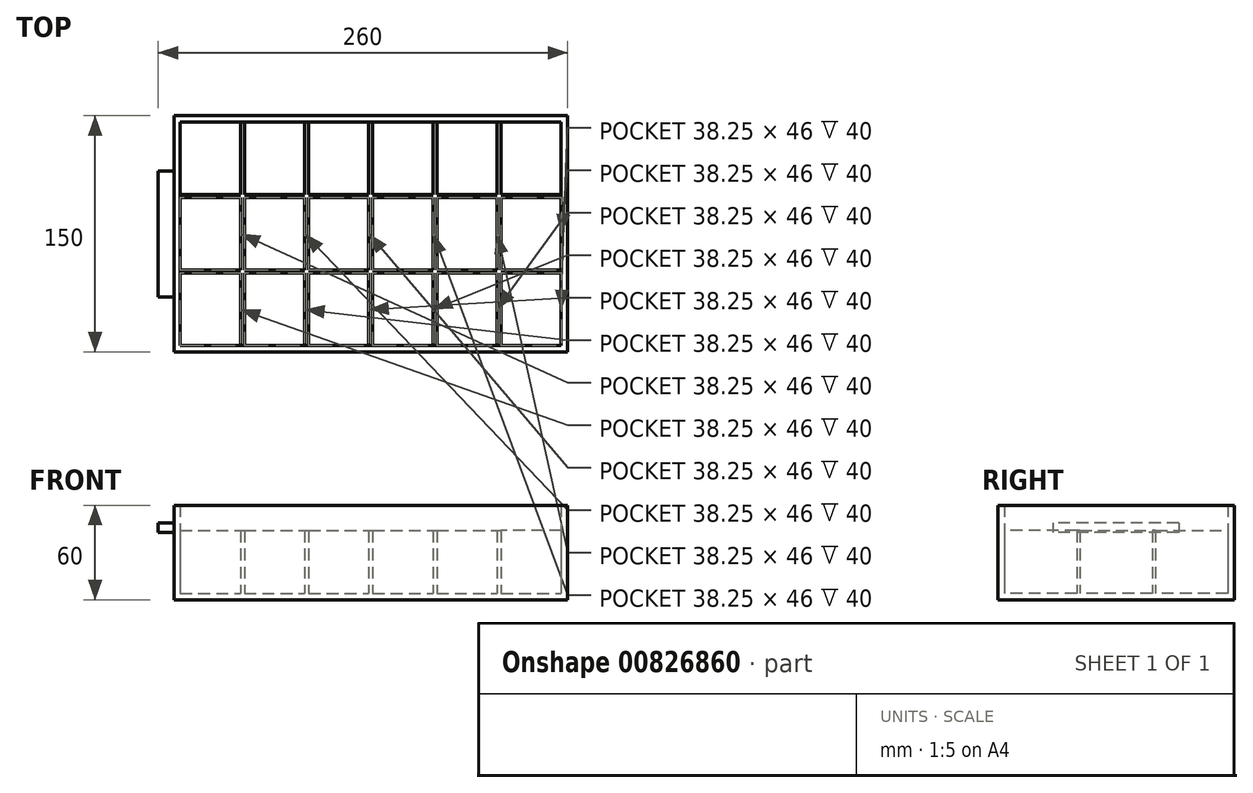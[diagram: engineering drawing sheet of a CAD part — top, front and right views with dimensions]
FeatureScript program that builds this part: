
annotation { "Feature Type Name" : "Feature", "Feature Type Description" : "" }
export const myFeature = defineFeature(function(context is Context, id is Id, definition is map)
    precondition{}
    {
        {
            var Q0;
            Q0=qCreatedBy(makeId("Top.planeOp"),FACE);
            var sketch = newSketch(context, id + "F0", { "sketchPlane" : qUnion([Q0])});
            skLineSegment(sketch, "E0.bottom", {"start": v(-124.11, 65.2) * mm, "end": v(125.89, 65.2) * mm});
            skLineSegment(sketch, "E0.top", {"start": v(-124.11, -84.8) * mm, "end": v(125.89, -84.8) * mm});
            skLineSegment(sketch, "E0.left", {"start": v(-124.11, 65.2) * mm, "end": v(-124.11, -84.8) * mm});
            skLineSegment(sketch, "E0.right", {"start": v(125.89, 65.2) * mm, "end": v(125.89, -84.8) * mm});
            skSolve(sketch);
        }
        {
            var Q0;
            Q0=makeQuery(id+"F0.imprint","IMPRINT",FACE,{"disambiguationData":[TD([[makeQuery(id+"F0.imprint","IMPRINT",EDGE,{"derivedFrom":sQuery(id+"F0.wireOp",EDGE,"E0.bottom")}),-1.0]])]});
            extrude(context, id + "F1", {"entities" : qUnion([Q0]), "depth" : 60 * mm, "offsetDistance" : 25 * mm});
        }
        {
            var Q0;
            Q0=makeQuery(id+"F1.opExtrude","CAP_FACE",FACE,{"disambiguationData":[OSD([sQuery(id+"F0.wireOp",EDGE,"E0.bottom"),sQuery(id+"F0.wireOp",EDGE,"E0.top"),sQuery(id+"F0.wireOp",EDGE,"E0.left"),sQuery(id+"F0.wireOp",EDGE,"E0.right")])],"isStart":false});
            shell(context, id + "F2", {"entities" : qUnion([Q0]), "thickness" : 4 * mm});
        }
        {
            var Q0;
            Q0=makeQuery(id+"F2.opShell","OFFSET_FACE",FACE,{"disambiguationData":[OSD([sQuery(id+"F0.wireOp",EDGE,"E0.bottom"),sQuery(id+"F0.wireOp",EDGE,"E0.top"),sQuery(id+"F0.wireOp",EDGE,"E0.left"),sQuery(id+"F0.wireOp",EDGE,"E0.right")])]});
            var sketch = newSketch(context, id + "F3", { "sketchPlane" : qUnion([Q0])});
            skLineSegment(sketch, "E1", {"start": v(-120.11, 15.2) * mm, "end": v(-81.86, 15.2) * mm});
            skLineSegment(sketch, "E2", {"start": v(-120.11, 13.2) * mm, "end": v(-81.86, 13.2) * mm});
            skLineSegment(sketch, "E3", {"start": v(-120.11, -32.8) * mm, "end": v(-81.86, -32.8) * mm});
            skLineSegment(sketch, "E4", {"start": v(121.89, -32.8) * mm, "end": v(121.89, -34.8) * mm});
            skLineSegment(sketch, "E5", {"start": v(121.89, -34.8) * mm, "end": v(83.64, -34.8) * mm});
            skLineSegment(sketch, "E6", {"start": v(-120.11, -34.8) * mm, "end": v(-120.11, -32.8) * mm});
            skLineSegment(sketch, "E7", {"start": v(-120.11, 15.2) * mm, "end": v(-120.11, 13.2) * mm});
            skLineSegment(sketch, "E8", {"start": v(121.89, 15.2) * mm, "end": v(121.89, 13.2) * mm});
            skLineSegment(sketch, "E9", {"start": v(-81.86, 61.2) * mm, "end": v(-81.86, 15.2) * mm});
            skLineSegment(sketch, "E10", {"start": v(-81.86, -80.8) * mm, "end": v(-79.36, -80.8) * mm});
            skLineSegment(sketch, "E11", {"start": v(-79.36, -80.8) * mm, "end": v(-79.36, -34.8) * mm});
            skLineSegment(sketch, "E12", {"start": v(-79.36, 61.2) * mm, "end": v(-81.86, 61.2) * mm});
            skLineSegment(sketch, "E13", {"start": v(-41.11, 61.2) * mm, "end": v(-41.11, 15.2) * mm});
            skLineSegment(sketch, "E14", {"start": v(-41.11, -80.8) * mm, "end": v(-38.61, -80.8) * mm});
            skLineSegment(sketch, "E15", {"start": v(-38.61, -80.8) * mm, "end": v(-38.61, -34.8) * mm});
            skLineSegment(sketch, "E16", {"start": v(-38.61, 61.2) * mm, "end": v(-41.11, 61.2) * mm});
            skLineSegment(sketch, "E17", {"start": v(-0.36, 61.2) * mm, "end": v(-0.36, 15.2) * mm});
            skLineSegment(sketch, "E18", {"start": v(-0.36, -80.8) * mm, "end": v(2.14, -80.8) * mm});
            skLineSegment(sketch, "E19", {"start": v(2.14, -80.8) * mm, "end": v(2.14, -34.8) * mm});
            skLineSegment(sketch, "E20", {"start": v(2.14, 61.2) * mm, "end": v(-0.36, 61.2) * mm});
            skLineSegment(sketch, "E21", {"start": v(40.39, 61.2) * mm, "end": v(40.39, 15.2) * mm});
            skLineSegment(sketch, "E22", {"start": v(40.39, -80.8) * mm, "end": v(42.89, -80.8) * mm});
            skLineSegment(sketch, "E23", {"start": v(42.89, -80.8) * mm, "end": v(42.89, -34.8) * mm});
            skLineSegment(sketch, "E24", {"start": v(42.89, 61.2) * mm, "end": v(40.39, 61.2) * mm});
            skLineSegment(sketch, "E25", {"start": v(81.14, 61.2) * mm, "end": v(81.14, 15.2) * mm});
            skLineSegment(sketch, "E26", {"start": v(81.14, -80.8) * mm, "end": v(83.64, -80.8) * mm});
            skLineSegment(sketch, "E27", {"start": v(83.64, -80.8) * mm, "end": v(83.64, -34.8) * mm});
            skLineSegment(sketch, "E28", {"start": v(83.64, 61.2) * mm, "end": v(81.14, 61.2) * mm});
            skLineSegment(sketch, "E29", {"start": v(-81.86, 13.2) * mm, "end": v(-81.86, -32.8) * mm});
            skLineSegment(sketch, "E30", {"start": v(-79.36, 15.2) * mm, "end": v(-41.11, 15.2) * mm});
            skLineSegment(sketch, "E31", {"start": v(-79.36, 13.2) * mm, "end": v(-41.11, 13.2) * mm});
            skLineSegment(sketch, "E32.trimOffspring", {"start": v(-79.36, 15.2) * mm, "end": v(-79.36, 61.2) * mm});
            skLineSegment(sketch, "E33", {"start": v(-38.61, 15.2) * mm, "end": v(-0.36, 15.2) * mm});
            skLineSegment(sketch, "E34", {"start": v(-38.61, 13.2) * mm, "end": v(-0.36, 13.2) * mm});
            skLineSegment(sketch, "E35", {"start": v(2.14, 15.2) * mm, "end": v(2.15, 15.2) * mm});
            skLineSegment(sketch, "E36", {"start": v(2.15, 15.2) * mm, "end": v(40.39, 15.2) * mm});
            skLineSegment(sketch, "E37", {"start": v(-0.36, 13.2) * mm, "end": v(-0.36, -32.8) * mm});
            skLineSegment(sketch, "E38", {"start": v(2.14, 13.2) * mm, "end": v(40.39, 13.2) * mm});
            skLineSegment(sketch, "E39", {"start": v(40.39, 13.2) * mm, "end": v(40.39, -32.8) * mm});
            skLineSegment(sketch, "E40", {"start": v(42.89, 15.2) * mm, "end": v(81.14, 15.2) * mm});
            skLineSegment(sketch, "E41", {"start": v(42.89, 13.2) * mm, "end": v(81.14, 13.2) * mm});
            skLineSegment(sketch, "E42", {"start": v(83.64, 15.2) * mm, "end": v(121.89, 15.2) * mm});
            skLineSegment(sketch, "E43", {"start": v(83.64, 15.2) * mm, "end": v(83.64, 61.2) * mm});
            skLineSegment(sketch, "E44", {"start": v(83.64, 13.2) * mm, "end": v(121.89, 13.2) * mm});
            skLineSegment(sketch, "E45", {"start": v(83.64, -32.8) * mm, "end": v(121.89, -32.8) * mm});
            skLineSegment(sketch, "E46", {"start": v(81.14, -34.8) * mm, "end": v(81.14, -80.8) * mm});
            skLineSegment(sketch, "E47", {"start": v(81.14, -34.8) * mm, "end": v(42.89, -34.8) * mm});
            skLineSegment(sketch, "E48", {"start": v(42.89, -32.8) * mm, "end": v(81.14, -32.8) * mm});
            skLineSegment(sketch, "E49", {"start": v(42.89, -32.8) * mm, "end": v(42.89, 13.2) * mm});
            skLineSegment(sketch, "E50", {"start": v(40.39, -34.8) * mm, "end": v(40.39, -80.8) * mm});
            skLineSegment(sketch, "E51", {"start": v(2.14, -32.8) * mm, "end": v(40.39, -32.8) * mm});
            skLineSegment(sketch, "E52", {"start": v(-0.36, -34.8) * mm, "end": v(-38.61, -34.8) * mm});
            skLineSegment(sketch, "E53", {"start": v(-0.36, -34.8) * mm, "end": v(-0.36, -80.8) * mm});
            skLineSegment(sketch, "E54", {"start": v(-38.61, -32.8) * mm, "end": v(-0.36, -32.8) * mm});
            skLineSegment(sketch, "E55", {"start": v(-41.11, -34.8) * mm, "end": v(-79.36, -34.8) * mm});
            skLineSegment(sketch, "E56", {"start": v(-41.11, -34.8) * mm, "end": v(-41.11, -80.8) * mm});
            skLineSegment(sketch, "E57", {"start": v(-79.36, -32.8) * mm, "end": v(-41.11, -32.8) * mm});
            skLineSegment(sketch, "E58", {"start": v(-79.36, -32.8) * mm, "end": v(-79.36, 13.2) * mm});
            skLineSegment(sketch, "E59", {"start": v(-81.86, -34.8) * mm, "end": v(-120.11, -34.8) * mm});
            skLineSegment(sketch, "E60.trimOffspring", {"start": v(-81.86, -34.8) * mm, "end": v(-81.86, -80.8) * mm});
            skLineSegment(sketch, "E61.trimOffspring", {"start": v(-38.61, -32.8) * mm, "end": v(-38.61, 13.2) * mm});
            skLineSegment(sketch, "E62.trimOffspring", {"start": v(2.14, -32.8) * mm, "end": v(2.14, 13.2) * mm});
            skLineSegment(sketch, "E63.trimOffspring", {"start": v(40.39, -34.8) * mm, "end": v(2.14, -34.8) * mm});
            skLineSegment(sketch, "E64.trimOffspring", {"start": v(83.64, -32.8) * mm, "end": v(83.64, 13.2) * mm});
            skLineSegment(sketch, "E65.trimOffspring", {"start": v(81.14, 13.2) * mm, "end": v(81.14, -32.8) * mm});
            skLineSegment(sketch, "E66.trimOffspring", {"start": v(42.89, 15.2) * mm, "end": v(42.89, 61.2) * mm});
            skLineSegment(sketch, "E67.trimOffspring", {"start": v(2.14, 15.2) * mm, "end": v(2.14, 61.2) * mm});
            skLineSegment(sketch, "E68.trimOffspring", {"start": v(-41.11, 13.2) * mm, "end": v(-41.11, -32.8) * mm});
            skLineSegment(sketch, "E69.trimOffspring", {"start": v(-38.61, 15.2) * mm, "end": v(-38.61, 61.2) * mm});
            skSolve(sketch);
        }
        {
            var Q0;
            Q0=makeQuery(id+"F3.imprint","IMPRINT",FACE,{"disambiguationData":[TD([[makeQuery(id+"F3.imprint","IMPRINT",EDGE,{"derivedFrom":sQuery(id+"F3.wireOp",EDGE,"E1")}),-1.0]])]});
            extrude(context, id + "F4", {"entities" : qUnion([Q0]), "operationType" : NewBodyOperationType.ADD, "depth" : 40 * mm, "offsetDistance" : 25 * mm});
        }
        {
            var Q0;
            Q0=makeQuery(id+"F1.opExtrude","SWEPT_FACE",FACE,{"disambiguationData":[OSD([sQuery(id+"F0.wireOp",EDGE,"E0.left")])]});
            var sketch = newSketch(context, id + "F5", { "sketchPlane" : qUnion([Q0])});
            skLineSegment(sketch, "E70.bottom", {"start": v(-30, 48.68) * mm, "end": v(50, 48.68) * mm});
            skLineSegment(sketch, "E70.top", {"start": v(-30, 42.68) * mm, "end": v(50, 42.68) * mm});
            skLineSegment(sketch, "E70.left", {"start": v(-30, 48.68) * mm, "end": v(-30, 42.68) * mm});
            skLineSegment(sketch, "E70.right", {"start": v(50, 48.68) * mm, "end": v(50, 42.68) * mm});
            skSolve(sketch);
        }
        {
            var Q0;
            Q0=makeQuery(id+"F5.imprint","IMPRINT",FACE,{"disambiguationData":[TD([[makeQuery(id+"F5.imprint","IMPRINT",EDGE,{"derivedFrom":sQuery(id+"F5.wireOp",EDGE,"E70.bottom")}),-1.0]])]});
            extrude(context, id + "F6", {"entities" : qUnion([Q0]), "operationType" : NewBodyOperationType.ADD, "depth" : 10 * mm, "offsetDistance" : 25 * mm});
        }
    });
